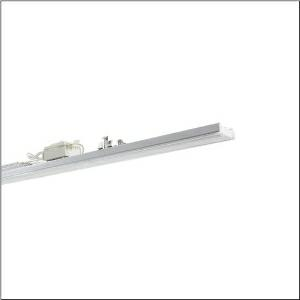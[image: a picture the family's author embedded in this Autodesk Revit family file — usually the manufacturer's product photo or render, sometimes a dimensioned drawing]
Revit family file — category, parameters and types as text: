
# Revit family: licross_r__11_recessed_ho_51te18dn4d5m_683b
name_source: partatom
category: Lighting Fixtures
units: mm (PartAtom-declared; Revit-internal decimal feet)

## family parameters
Cut with Voids When Loaded = No
Host = Face
Light Source = No
Part Type = Normal
Room Calculation Point = No
Round Connector Dimension = Use Diameter
Shared = No

## types (1)
- --- (1 x LED, 13890 lm, 76.8 W, 4000K)
    Apparent Load = 77 VA
    CIE Flux Codes = 78 94 99 100 100
    Color Rendering = 80
    Color Temperature = 4000K
    Default Elevation = 1800 mm
    Description = Licross® 11 Recessed HO, luminaire insert, of sheet steel, galvanised, coil coated, white, length: 1.500mm, width: 66mm, height: 67mm, LED rated luminous flux: 13.890lm, light colour: 840, control gear: DALI 2, with plug, 5-pole, with phase selection, mains connection: 220..240V, AC, 50/60Hz, rated input power: 77W, halogen-free wiring, primary light control with lens, of plastic, primary optical cover: cover, of PMMA, light emission: direct distribution, primary light characteristic: symmetric, protection rating (complete): IP54, insulation class (complete): insulation class I (protective earthing), certification: CE, ENEC, VDE, UKCA, protection symbol: D if used in an environment with non-conductive dust loads with corresponding accessories, impact resistance: IK06, permissible ambient temperature for indoor applications: -25..+30°C, corresponds to IFS (International Featured Standards) requirements for safety and quality in the food industry, reducing of maximum allowable ambient temperature of 5°C with ceiling mounting, LABS conformity tested according to VDMA 24364:2018-05, packaging unit: 1 piece
    Height = 58 mm
    Lamp = 1 x LED
    Lamp Light Flux = 13890 lm
    Lamp Power = 76.8 W
    Lamp count = 1
    Length = 1500 mm
    Luminous efficacy = 181 lm/W
    Manufacturer = Siteco
    ModVariant = No
    Model = 51TE18DN4D5M
    Mounting Place = Ceiling
    Mounting Type = Pendant
    Number of Poles = 1
    OnlyDefault = Yes
    Power Factor = 1
    Product Name = Licross® 11 Recessed HO
    Product group = luminaire insert
    ProductGroupID = 902
    Protection Class = Protection class I
    Protection Degree = IP 54
    RLX_Detail_Level = 1
    RLX_Emergency_Light_Flux = 0 lm
    RLX_Emergency_Type = 0
    RLX_Emergency_Type_DB = No
    RlxData = <blob elided: 24625 chars, md5=85fa0514>
    Socket = socket
    Standby Power = 0 W
    System Light Flux = 13890 lm
    System Power = 77 W
    Type Comments = factory setting: luminous flux: 100 % | dim-lin: 254 | 522 mA
    Type Image = l_1296930.jpg
    URL = http://relux.com
    VarID = @adj_099404
    Voltage = 0 V
    Weight = 0.00 kg
    Width = 66 mm

## geometry (parser evidence)
native form markers: Blend x4, Sweep x11
no freeform markers — native parametric forms only
